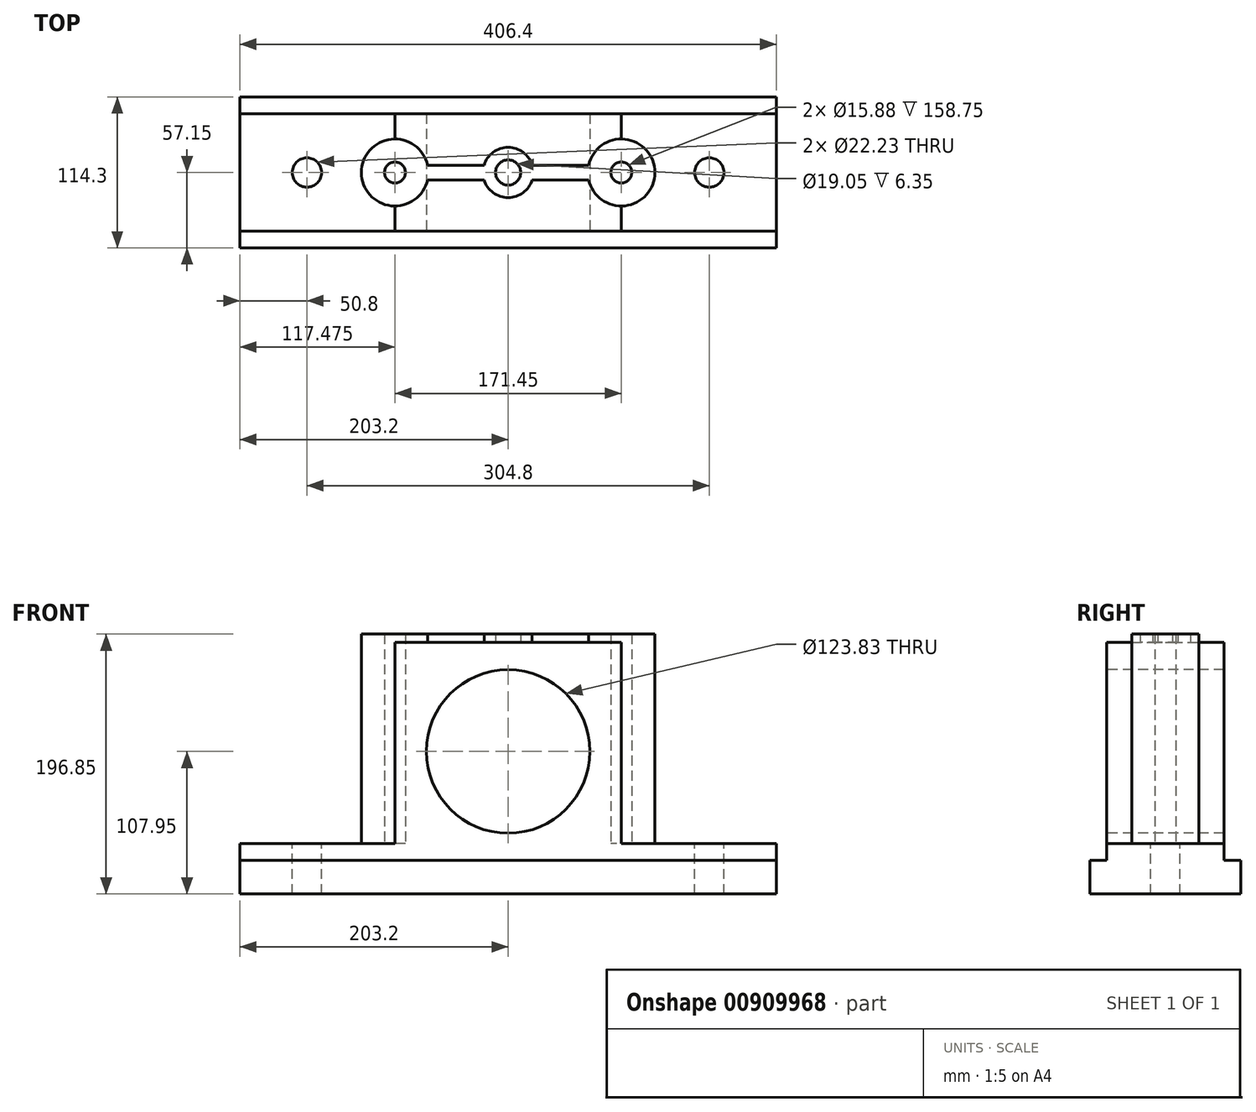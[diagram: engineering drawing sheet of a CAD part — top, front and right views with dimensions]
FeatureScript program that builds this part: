
annotation { "Feature Type Name" : "Feature", "Feature Type Description" : "" }
export const myFeature = defineFeature(function(context is Context, id is Id, definition is map)
    precondition{}
    {
        {
            var Q0;
            Q0=qCreatedBy(makeId("Front.planeOp"),FACE);
            var sketch = newSketch(context, id + "F0", { "sketchPlane" : qUnion([Q0])});
            skLineSegment(sketch, "E0.bottom", {"start": v(-203.2, 0) * mm, "end": v(203.2, 0) * mm});
            skLineSegment(sketch, "E0.top", {"start": v(-203.2, 25.4) * mm, "end": v(203.2, 25.4) * mm});
            skLineSegment(sketch, "E0.left", {"start": v(-203.2, 0) * mm, "end": v(-203.2, 25.4) * mm});
            skLineSegment(sketch, "E0.right", {"start": v(203.2, 0) * mm, "end": v(203.2, 25.4) * mm});
            skLineSegment(sketch, "E1", {"start": v(-203.2, 25.4) * mm, "end": v(-203.2, 38.1) * mm});
            skLineSegment(sketch, "E2", {"start": v(-203.2, 38.1) * mm, "end": v(203.2, 38.1) * mm});
            skLineSegment(sketch, "E3", {"start": v(203.2, 38.1) * mm, "end": v(203.2, 25.4) * mm});
            skLineSegment(sketch, "E4", {"start": v(0, 38.1) * mm, "end": v(0, 0) * mm, "construction": true});
            skCircle(sketch, "E5", {"center": v(0, 107.95) * mm, "radius": 61.91 * mm});
            skSolve(sketch);
        }
        {
            var Q0;
            Q0=makeQuery(id+"F0.imprint","IMPRINT",FACE,{"disambiguationData":[TD([[makeQuery(id+"F0.imprint","IMPRINT",EDGE,{"derivedFrom":sQuery(id+"F0.wireOp",EDGE,"E0.bottom")}),1.0]])]});
            extrude(context, id + "F1", {"entities" : qUnion([Q0]), "depth" : 114.3 * mm, "offsetDistance" : 25 * mm, "symmetric" : true});
        }
        {
            var Q0;
            Q0=makeQuery(id+"F0.imprint","IMPRINT",FACE,{"disambiguationData":[TD([[makeQuery(id+"F0.imprint","IMPRINT",EDGE,{"derivedFrom":sQuery(id+"F0.wireOp",EDGE,"E0.top")}),1.0]])]});
            extrude(context, id + "F2", {"entities" : qUnion([Q0]), "operationType" : NewBodyOperationType.ADD, "depth" : 88.9 * mm, "offsetDistance" : 25 * mm, "symmetric" : true});
        }
        {
            var Q0;
            Q0=makeQuery(id+"F2.opExtrude","SWEPT_FACE",FACE,{"disambiguationData":[OSD([sQuery(id+"F0.wireOp",EDGE,"E2")])]});
            var sketch = newSketch(context, id + "F3", { "sketchPlane" : qUnion([Q0])});
            skLineSegment(sketch, "E6.bottom", {"start": v(-85.72, 44.45) * mm, "end": v(85.72, 44.45) * mm});
            skLineSegment(sketch, "E6.top", {"start": v(-85.72, -44.45) * mm, "end": v(85.72, -44.45) * mm});
            skLineSegment(sketch, "E6.left", {"start": v(-85.72, 44.45) * mm, "end": v(-85.72, -44.45) * mm});
            skLineSegment(sketch, "E6.right", {"start": v(85.72, 44.45) * mm, "end": v(85.72, -44.45) * mm});
            skCircle(sketch, "E7", {"center": v(-85.72, 0) * mm, "radius": 25.4 * mm});
            skCircle(sketch, "E8", {"center": v(85.72, 0) * mm, "radius": 25.4 * mm});
            skCircle(sketch, "E9", {"center": v(0, 0) * mm, "radius": 19.05 * mm});
            skCircle(sketch, "E10", {"center": v(-85.72, 0) * mm, "radius": 7.94 * mm});
            skCircle(sketch, "E11", {"center": v(85.72, 0) * mm, "radius": 7.94 * mm});
            skCircle(sketch, "E12", {"center": v(0, 0) * mm, "radius": 9.53 * mm});
            skLineSegment(sketch, "E13", {"start": v(-60.94, 5.56) * mm, "end": v(-18.22, 5.56) * mm});
            skLineSegment(sketch, "E14", {"start": v(18.22, 5.56) * mm, "end": v(60.94, 5.56) * mm});
            skLineSegment(sketch, "E15", {"start": v(-60.94, -5.56) * mm, "end": v(-18.22, -5.56) * mm});
            skLineSegment(sketch, "E16", {"start": v(18.22, -5.56) * mm, "end": v(60.94, -5.56) * mm});
            skCircle(sketch, "E17", {"center": v(-152.4, 0) * mm, "radius": 11.11 * mm});
            skCircle(sketch, "E18", {"center": v(152.4, 0) * mm, "radius": 11.11 * mm});
            skLineSegment(sketch, "E19", {"start": v(-152.4, 0) * mm, "end": v(0, 0) * mm, "construction": true});
            skLineSegment(sketch, "E20", {"start": v(0, 0) * mm, "end": v(152.4, 0) * mm, "construction": true});
            skLineSegment(sketch, "E21", {"start": v(-69.85, 44.45) * mm, "end": v(-69.85, -44.45) * mm});
            skLineSegment(sketch, "E22", {"start": v(69.85, 44.45) * mm, "end": v(69.85, -44.45) * mm});
            skSolve(sketch);
        }
        {
            var Q0;
            {var subQ0=sQuery(id+"F3.wireOp",EDGE,"E7");var subQ1=sQuery(id+"F3.wireOp",EDGE,"E6.left");var subQ2=makeQuery(id+"F3.imprint","INTERSECT",VERTEX,{"disambiguationData":[OD(0.0)],"derivedFrom":[subQ1,subQ0]});Q0=makeQuery(id+"F3.imprint","IMPRINT",FACE,{"disambiguationData":[TD([[makeQuery(id+"F3.imprint","IMPRINT",EDGE,{"disambiguationData":[TD([[subQ2,-1.0]])],"derivedFrom":subQ1}),-1.0]])]});}
            var Q1;
            {var subQ0=sQuery(id+"F3.wireOp",EDGE,"E7");var subQ2=sQuery(id+"F3.wireOp",EDGE,"E6.left");var subQ4=makeQuery(id+"F3.imprint","INTERSECT",VERTEX,{"disambiguationData":[OD(0.0)],"derivedFrom":[subQ2,subQ0]});Q1=makeQuery(id+"F3.imprint","IMPRINT",FACE,{"disambiguationData":[TD([[makeQuery(id+"F3.imprint","IMPRINT",EDGE,{"disambiguationData":[TD([[subQ4,-1.0]])],"derivedFrom":subQ2}),1.0]])]});}
            var Q2;
            {var subQ0=sQuery(id+"F3.wireOp",EDGE,"E13");Q2=makeQuery(id+"F3.imprint","IMPRINT",FACE,{"disambiguationData":[TD([[makeQuery(id+"F3.imprint","IMPRINT",EDGE,{"derivedFrom":subQ0}),-1.0]])]});}
            var Q3;
            Q3=makeQuery(id+"F3.imprint","IMPRINT",FACE,{"disambiguationData":[TD([[makeQuery(id+"F3.imprint","IMPRINT",EDGE,{"derivedFrom":sQuery(id+"F3.wireOp",EDGE,"E12")}),-1.0]])]});
            var Q4;
            {var subQ0=sQuery(id+"F3.wireOp",EDGE,"E14");Q4=makeQuery(id+"F3.imprint","IMPRINT",FACE,{"disambiguationData":[TD([[makeQuery(id+"F3.imprint","IMPRINT",EDGE,{"derivedFrom":subQ0}),-1.0]])]});}
            var Q5;
            {var subQ0=sQuery(id+"F3.wireOp",EDGE,"E8");var subQ3=sQuery(id+"F3.wireOp",EDGE,"E6.right");var subQ4=makeQuery(id+"F3.imprint","INTERSECT",VERTEX,{"disambiguationData":[OD(0.0)],"derivedFrom":[subQ3,subQ0]});Q5=makeQuery(id+"F3.imprint","IMPRINT",FACE,{"disambiguationData":[TD([[makeQuery(id+"F3.imprint","IMPRINT",EDGE,{"disambiguationData":[TD([[subQ4,-1.0]])],"derivedFrom":subQ3}),-1.0]])]});}
            var Q6;
            {var subQ0=sQuery(id+"F3.wireOp",EDGE,"E8");var subQ1=sQuery(id+"F3.wireOp",EDGE,"E6.right");var subQ2=makeQuery(id+"F3.imprint","INTERSECT",VERTEX,{"disambiguationData":[OD(0.0)],"derivedFrom":[subQ1,subQ0]});Q6=makeQuery(id+"F3.imprint","IMPRINT",FACE,{"disambiguationData":[TD([[makeQuery(id+"F3.imprint","IMPRINT",EDGE,{"disambiguationData":[TD([[subQ2,-1.0]])],"derivedFrom":subQ1}),1.0]])]});}
            var Q7;
            {var subQ0=sQuery(id+"F3.wireOp",EDGE,"E7");var subQ1=makeQuery(id+"F3.imprint","INTERSECT",VERTEX,{"derivedFrom":[subQ0,sQuery(id+"F3.wireOp",EDGE,"E13")]});Q7=makeQuery(id+"F3.imprint","IMPRINT",FACE,{"disambiguationData":[TD([[makeQuery(id+"F3.imprint","IMPRINT",EDGE,{"disambiguationData":[TD([[subQ1,-1.0]])],"derivedFrom":subQ0}),1.0]])]});}
            var Q8;
            {var subQ0=sQuery(id+"F3.wireOp",EDGE,"E8");var subQ1=makeQuery(id+"F3.imprint","INTERSECT",VERTEX,{"derivedFrom":[subQ0,sQuery(id+"F3.wireOp",EDGE,"E14")]});Q8=makeQuery(id+"F3.imprint","IMPRINT",FACE,{"disambiguationData":[TD([[makeQuery(id+"F3.imprint","IMPRINT",EDGE,{"disambiguationData":[TD([[subQ1,1.0]])],"derivedFrom":subQ0}),1.0]])]});}
            extrude(context, id + "F4", {"entities" : qUnion([Q0, Q1, Q2, Q3, Q4, Q5, Q6, Q7, Q8]), "depth" : 158.75 * mm, "offsetDistance" : 25 * mm});
        }
        {
            var Q0;
            {var subQ5=sQuery(id+"F3.wireOp",EDGE,"E6.bottom");Q0=makeQuery(id+"F3.imprint","IMPRINT",FACE,{"disambiguationData":[TD([[makeQuery(id+"F3.imprint","IMPRINT",EDGE,{"derivedFrom":subQ5}),-1.0]])]});}
            var Q1;
            {var subQ5=sQuery(id+"F3.wireOp",EDGE,"E6.top");Q1=makeQuery(id+"F3.imprint","IMPRINT",FACE,{"disambiguationData":[TD([[makeQuery(id+"F3.imprint","IMPRINT",EDGE,{"derivedFrom":subQ5}),1.0]])]});}
            var Q2;
            Q2=makeQuery(id+"F3.imprint","IMPRINT",FACE,{"disambiguationData":[TD([[makeQuery(id+"F3.imprint","IMPRINT",EDGE,{"derivedFrom":sQuery(id+"F3.wireOp",EDGE,"E12")}),1.0]])]});
            var Q3;
            {var subQ0=sQuery(id+"F3.wireOp",EDGE,"E15");Q3=makeQuery(id+"F3.imprint","IMPRINT",FACE,{"disambiguationData":[TD([[makeQuery(id+"F3.imprint","IMPRINT",EDGE,{"derivedFrom":subQ0}),-1.0]])]});}
            var Q4;
            {var subQ0=sQuery(id+"F3.wireOp",EDGE,"E13");Q4=makeQuery(id+"F3.imprint","IMPRINT",FACE,{"disambiguationData":[TD([[makeQuery(id+"F3.imprint","IMPRINT",EDGE,{"derivedFrom":subQ0}),1.0]])]});}
            extrude(context, id + "F5", {"entities" : qUnion([Q0, Q1, Q2, Q3, Q4]), "operationType" : NewBodyOperationType.ADD, "depth" : 152.4 * mm, "offsetDistance" : 25 * mm});
        }
        {
            var Q0;
            {var subQ0=sQuery(id+"F3.wireOp",EDGE,"E13");Q0=makeQuery(id+"F3.imprint","IMPRINT",FACE,{"disambiguationData":[TD([[makeQuery(id+"F3.imprint","IMPRINT",EDGE,{"derivedFrom":subQ0}),1.0]])]});}
            var Q1;
            {var subQ0=sQuery(id+"F3.wireOp",EDGE,"E15");Q1=makeQuery(id+"F3.imprint","IMPRINT",FACE,{"disambiguationData":[TD([[makeQuery(id+"F3.imprint","IMPRINT",EDGE,{"derivedFrom":subQ0}),-1.0]])]});}
            var Q2;
            {var subQ0=sQuery(id+"F3.wireOp",EDGE,"E7");var subQ1=makeQuery(id+"F3.imprint","INTERSECT",VERTEX,{"derivedFrom":[subQ0,sQuery(id+"F3.wireOp",EDGE,"E13")]});Q2=makeQuery(id+"F3.imprint","IMPRINT",FACE,{"disambiguationData":[TD([[makeQuery(id+"F3.imprint","IMPRINT",EDGE,{"disambiguationData":[TD([[subQ1,-1.0]])],"derivedFrom":subQ0}),1.0]])]});}
            var Q3;
            {var subQ0=sQuery(id+"F3.wireOp",EDGE,"E13");Q3=makeQuery(id+"F3.imprint","IMPRINT",FACE,{"disambiguationData":[TD([[makeQuery(id+"F3.imprint","IMPRINT",EDGE,{"derivedFrom":subQ0}),-1.0]])]});}
            var Q4;
            Q4=makeQuery(id+"F3.imprint","IMPRINT",FACE,{"disambiguationData":[TD([[makeQuery(id+"F3.imprint","IMPRINT",EDGE,{"derivedFrom":sQuery(id+"F3.wireOp",EDGE,"E12")}),-1.0]])]});
            var Q5;
            Q5=makeQuery(id+"F3.imprint","IMPRINT",FACE,{"disambiguationData":[TD([[makeQuery(id+"F3.imprint","IMPRINT",EDGE,{"derivedFrom":sQuery(id+"F3.wireOp",EDGE,"E12")}),1.0]])]});
            var Q6;
            {var subQ0=sQuery(id+"F3.wireOp",EDGE,"E14");Q6=makeQuery(id+"F3.imprint","IMPRINT",FACE,{"disambiguationData":[TD([[makeQuery(id+"F3.imprint","IMPRINT",EDGE,{"derivedFrom":subQ0}),-1.0]])]});}
            var Q7;
            {var subQ0=sQuery(id+"F3.wireOp",EDGE,"E8");var subQ1=makeQuery(id+"F3.imprint","INTERSECT",VERTEX,{"derivedFrom":[subQ0,sQuery(id+"F3.wireOp",EDGE,"E14")]});Q7=makeQuery(id+"F3.imprint","IMPRINT",FACE,{"disambiguationData":[TD([[makeQuery(id+"F3.imprint","IMPRINT",EDGE,{"disambiguationData":[TD([[subQ1,1.0]])],"derivedFrom":subQ0}),1.0]])]});}
            extrude(context, id + "F6", {"entities" : qUnion([Q0, Q1, Q2, Q3, Q4, Q5, Q6, Q7]), "operationType" : NewBodyOperationType.REMOVE, "depth" : 69.85 * mm, "offsetDistance" : 25 * mm});
        }
        {
            var Q0;
            {var subQ0=sQuery(id+"F3.wireOp",EDGE,"E6.left");var subQ5=sQuery(id+"F3.wireOp",EDGE,"E7");var subQ6=makeQuery(id+"F3.imprint","INTERSECT",VERTEX,{"disambiguationData":[OD(0.0)],"derivedFrom":[subQ0,subQ5]});Q0=makeQuery(id+"F3.imprint","IMPRINT",FACE,{"disambiguationData":[TD([[makeQuery(id+"F3.imprint","IMPRINT",EDGE,{"disambiguationData":[TD([[subQ6,1.0]])],"derivedFrom":subQ5}),-1.0]])]});}
            var Q1;
            {var subQ0=sQuery(id+"F3.wireOp",EDGE,"E6.left");var subQ5=sQuery(id+"F3.wireOp",EDGE,"E7");var subQ6=makeQuery(id+"F3.imprint","INTERSECT",VERTEX,{"disambiguationData":[OD(1.0)],"derivedFrom":[subQ0,subQ5]});Q1=makeQuery(id+"F3.imprint","IMPRINT",FACE,{"disambiguationData":[TD([[makeQuery(id+"F3.imprint","IMPRINT",EDGE,{"disambiguationData":[TD([[subQ6,-1.0]])],"derivedFrom":subQ5}),-1.0]])]});}
            var Q2;
            {var subQ0=sQuery(id+"F3.wireOp",EDGE,"E7");var subQ1=sQuery(id+"F3.wireOp",EDGE,"E6.left");var subQ7=makeQuery(id+"F3.imprint","INTERSECT",VERTEX,{"disambiguationData":[OD(0.0)],"derivedFrom":[subQ1,subQ0]});Q2=makeQuery(id+"F3.imprint","IMPRINT",FACE,{"disambiguationData":[TD([[makeQuery(id+"F3.imprint","IMPRINT",EDGE,{"disambiguationData":[TD([[subQ7,-1.0]])],"derivedFrom":subQ1}),1.0]])]});}
            var Q3;
            {var subQ0=sQuery(id+"F3.wireOp",EDGE,"E7");var subQ1=sQuery(id+"F3.wireOp",EDGE,"E6.left");var subQ2=makeQuery(id+"F3.imprint","INTERSECT",VERTEX,{"disambiguationData":[OD(0.0)],"derivedFrom":[subQ1,subQ0]});Q3=makeQuery(id+"F3.imprint","IMPRINT",FACE,{"disambiguationData":[TD([[makeQuery(id+"F3.imprint","IMPRINT",EDGE,{"disambiguationData":[TD([[subQ2,-1.0]])],"derivedFrom":subQ1}),-1.0]])]});}
            var Q4;
            {var subQ0=sQuery(id+"F3.wireOp",EDGE,"E8");var subQ1=sQuery(id+"F3.wireOp",EDGE,"E6.right");var subQ2=makeQuery(id+"F3.imprint","INTERSECT",VERTEX,{"disambiguationData":[OD(0.0)],"derivedFrom":[subQ1,subQ0]});Q4=makeQuery(id+"F3.imprint","IMPRINT",FACE,{"disambiguationData":[TD([[makeQuery(id+"F3.imprint","IMPRINT",EDGE,{"disambiguationData":[TD([[subQ2,-1.0]])],"derivedFrom":subQ1}),1.0]])]});}
            var Q5;
            {var subQ0=sQuery(id+"F3.wireOp",EDGE,"E8");var subQ1=sQuery(id+"F3.wireOp",EDGE,"E6.right");var subQ8=makeQuery(id+"F3.imprint","INTERSECT",VERTEX,{"disambiguationData":[OD(0.0)],"derivedFrom":[subQ1,subQ0]});Q5=makeQuery(id+"F3.imprint","IMPRINT",FACE,{"disambiguationData":[TD([[makeQuery(id+"F3.imprint","IMPRINT",EDGE,{"disambiguationData":[TD([[subQ8,-1.0]])],"derivedFrom":subQ1}),-1.0]])]});}
            var Q6;
            {var subQ0=sQuery(id+"F3.wireOp",EDGE,"E6.right");var subQ5=sQuery(id+"F3.wireOp",EDGE,"E8");var subQ6=makeQuery(id+"F3.imprint","INTERSECT",VERTEX,{"disambiguationData":[OD(0.0)],"derivedFrom":[subQ0,subQ5]});Q6=makeQuery(id+"F3.imprint","IMPRINT",FACE,{"disambiguationData":[TD([[makeQuery(id+"F3.imprint","IMPRINT",EDGE,{"disambiguationData":[TD([[subQ6,-1.0]])],"derivedFrom":subQ5}),-1.0]])]});}
            var Q7;
            {var subQ0=sQuery(id+"F3.wireOp",EDGE,"E6.right");var subQ5=sQuery(id+"F3.wireOp",EDGE,"E8");var subQ6=makeQuery(id+"F3.imprint","INTERSECT",VERTEX,{"disambiguationData":[OD(1.0)],"derivedFrom":[subQ0,subQ5]});Q7=makeQuery(id+"F3.imprint","IMPRINT",FACE,{"disambiguationData":[TD([[makeQuery(id+"F3.imprint","IMPRINT",EDGE,{"disambiguationData":[TD([[subQ6,1.0]])],"derivedFrom":subQ5}),-1.0]])]});}
            extrude(context, id + "F7", {"entities" : qUnion([Q0, Q1, Q2, Q3, Q4, Q5, Q6, Q7]), "operationType" : NewBodyOperationType.REMOVE, "depth" : 127 * mm, "offsetDistance" : 25 * mm});
        }
        {
            var Q0;
            {var subQ0=sQuery(id+"F3.wireOp",EDGE,"E6.left");var subQ5=sQuery(id+"F3.wireOp",EDGE,"E7");var subQ6=makeQuery(id+"F3.imprint","INTERSECT",VERTEX,{"disambiguationData":[OD(0.0)],"derivedFrom":[subQ0,subQ5]});Q0=makeQuery(id+"F3.imprint","IMPRINT",FACE,{"disambiguationData":[TD([[makeQuery(id+"F3.imprint","IMPRINT",EDGE,{"disambiguationData":[TD([[subQ6,1.0]])],"derivedFrom":subQ5}),-1.0]])]});}
            var Q1;
            {var subQ0=sQuery(id+"F3.wireOp",EDGE,"E7");var subQ1=sQuery(id+"F3.wireOp",EDGE,"E6.left");var subQ2=makeQuery(id+"F3.imprint","INTERSECT",VERTEX,{"disambiguationData":[OD(0.0)],"derivedFrom":[subQ1,subQ0]});Q1=makeQuery(id+"F3.imprint","IMPRINT",FACE,{"disambiguationData":[TD([[makeQuery(id+"F3.imprint","IMPRINT",EDGE,{"disambiguationData":[TD([[subQ2,-1.0]])],"derivedFrom":subQ1}),-1.0]])]});}
            var Q2;
            {var subQ0=sQuery(id+"F3.wireOp",EDGE,"E7");var subQ1=sQuery(id+"F3.wireOp",EDGE,"E6.left");var subQ7=makeQuery(id+"F3.imprint","INTERSECT",VERTEX,{"disambiguationData":[OD(0.0)],"derivedFrom":[subQ1,subQ0]});Q2=makeQuery(id+"F3.imprint","IMPRINT",FACE,{"disambiguationData":[TD([[makeQuery(id+"F3.imprint","IMPRINT",EDGE,{"disambiguationData":[TD([[subQ7,-1.0]])],"derivedFrom":subQ1}),1.0]])]});}
            var Q3;
            {var subQ0=sQuery(id+"F3.wireOp",EDGE,"E6.left");var subQ5=sQuery(id+"F3.wireOp",EDGE,"E7");var subQ6=makeQuery(id+"F3.imprint","INTERSECT",VERTEX,{"disambiguationData":[OD(1.0)],"derivedFrom":[subQ0,subQ5]});Q3=makeQuery(id+"F3.imprint","IMPRINT",FACE,{"disambiguationData":[TD([[makeQuery(id+"F3.imprint","IMPRINT",EDGE,{"disambiguationData":[TD([[subQ6,-1.0]])],"derivedFrom":subQ5}),-1.0]])]});}
            var Q4;
            {var subQ0=sQuery(id+"F3.wireOp",EDGE,"E6.right");var subQ5=sQuery(id+"F3.wireOp",EDGE,"E8");var subQ6=makeQuery(id+"F3.imprint","INTERSECT",VERTEX,{"disambiguationData":[OD(1.0)],"derivedFrom":[subQ0,subQ5]});Q4=makeQuery(id+"F3.imprint","IMPRINT",FACE,{"disambiguationData":[TD([[makeQuery(id+"F3.imprint","IMPRINT",EDGE,{"disambiguationData":[TD([[subQ6,1.0]])],"derivedFrom":subQ5}),-1.0]])]});}
            var Q5;
            {var subQ0=sQuery(id+"F3.wireOp",EDGE,"E8");var subQ1=sQuery(id+"F3.wireOp",EDGE,"E6.right");var subQ8=makeQuery(id+"F3.imprint","INTERSECT",VERTEX,{"disambiguationData":[OD(0.0)],"derivedFrom":[subQ1,subQ0]});Q5=makeQuery(id+"F3.imprint","IMPRINT",FACE,{"disambiguationData":[TD([[makeQuery(id+"F3.imprint","IMPRINT",EDGE,{"disambiguationData":[TD([[subQ8,-1.0]])],"derivedFrom":subQ1}),-1.0]])]});}
            var Q6;
            {var subQ0=sQuery(id+"F3.wireOp",EDGE,"E8");var subQ1=sQuery(id+"F3.wireOp",EDGE,"E6.right");var subQ2=makeQuery(id+"F3.imprint","INTERSECT",VERTEX,{"disambiguationData":[OD(0.0)],"derivedFrom":[subQ1,subQ0]});Q6=makeQuery(id+"F3.imprint","IMPRINT",FACE,{"disambiguationData":[TD([[makeQuery(id+"F3.imprint","IMPRINT",EDGE,{"disambiguationData":[TD([[subQ2,-1.0]])],"derivedFrom":subQ1}),1.0]])]});}
            var Q7;
            {var subQ0=sQuery(id+"F3.wireOp",EDGE,"E6.right");var subQ5=sQuery(id+"F3.wireOp",EDGE,"E8");var subQ6=makeQuery(id+"F3.imprint","INTERSECT",VERTEX,{"disambiguationData":[OD(0.0)],"derivedFrom":[subQ0,subQ5]});Q7=makeQuery(id+"F3.imprint","IMPRINT",FACE,{"disambiguationData":[TD([[makeQuery(id+"F3.imprint","IMPRINT",EDGE,{"disambiguationData":[TD([[subQ6,-1.0]])],"derivedFrom":subQ5}),-1.0]])]});}
            extrude(context, id + "F8", {"entities" : qUnion([Q0, Q1, Q2, Q3, Q4, Q5, Q6, Q7]), "operationType" : NewBodyOperationType.ADD, "depth" : 127 * mm, "offsetDistance" : 25 * mm});
        }
        {
            var Q0;
            {var subQ0=sQuery(id+"F3.wireOp",EDGE,"E13");Q0=makeQuery(id+"F3.imprint","IMPRINT",FACE,{"disambiguationData":[TD([[makeQuery(id+"F3.imprint","IMPRINT",EDGE,{"derivedFrom":subQ0}),1.0]])]});}
            var Q1;
            {var subQ0=sQuery(id+"F3.wireOp",EDGE,"E7");var subQ1=makeQuery(id+"F3.imprint","INTERSECT",VERTEX,{"derivedFrom":[subQ0,sQuery(id+"F3.wireOp",EDGE,"E13")]});Q1=makeQuery(id+"F3.imprint","IMPRINT",FACE,{"disambiguationData":[TD([[makeQuery(id+"F3.imprint","IMPRINT",EDGE,{"disambiguationData":[TD([[subQ1,-1.0]])],"derivedFrom":subQ0}),1.0]])]});}
            var Q2;
            Q2=makeQuery(id+"F3.imprint","IMPRINT",FACE,{"disambiguationData":[TD([[makeQuery(id+"F3.imprint","IMPRINT",EDGE,{"derivedFrom":sQuery(id+"F3.wireOp",EDGE,"E12")}),-1.0]])]});
            var Q3;
            Q3=makeQuery(id+"F3.imprint","IMPRINT",FACE,{"disambiguationData":[TD([[makeQuery(id+"F3.imprint","IMPRINT",EDGE,{"derivedFrom":sQuery(id+"F3.wireOp",EDGE,"E12")}),1.0]])]});
            var Q4;
            {var subQ0=sQuery(id+"F3.wireOp",EDGE,"E8");var subQ1=makeQuery(id+"F3.imprint","INTERSECT",VERTEX,{"derivedFrom":[subQ0,sQuery(id+"F3.wireOp",EDGE,"E14")]});Q4=makeQuery(id+"F3.imprint","IMPRINT",FACE,{"disambiguationData":[TD([[makeQuery(id+"F3.imprint","IMPRINT",EDGE,{"disambiguationData":[TD([[subQ1,1.0]])],"derivedFrom":subQ0}),1.0]])]});}
            var Q5;
            {var subQ0=sQuery(id+"F3.wireOp",EDGE,"E14");Q5=makeQuery(id+"F3.imprint","IMPRINT",FACE,{"disambiguationData":[TD([[makeQuery(id+"F3.imprint","IMPRINT",EDGE,{"derivedFrom":subQ0}),-1.0]])]});}
            var Q6;
            {var subQ0=sQuery(id+"F3.wireOp",EDGE,"E13");Q6=makeQuery(id+"F3.imprint","IMPRINT",FACE,{"disambiguationData":[TD([[makeQuery(id+"F3.imprint","IMPRINT",EDGE,{"derivedFrom":subQ0}),-1.0]])]});}
            var Q7;
            {var subQ0=sQuery(id+"F3.wireOp",EDGE,"E15");Q7=makeQuery(id+"F3.imprint","IMPRINT",FACE,{"disambiguationData":[TD([[makeQuery(id+"F3.imprint","IMPRINT",EDGE,{"derivedFrom":subQ0}),-1.0]])]});}
            extrude(context, id + "F9", {"entities" : qUnion([Q0, Q1, Q2, Q3, Q4, Q5, Q6, Q7]), "operationType" : NewBodyOperationType.ADD, "depth" : 69.85 * mm, "offsetDistance" : 25 * mm});
        }
        {
            var Q0;
            Q0=makeQuery(id+"F3.imprint","IMPRINT",FACE,{"disambiguationData":[TD([[makeQuery(id+"F3.imprint","IMPRINT",EDGE,{"derivedFrom":sQuery(id+"F3.wireOp",EDGE,"E17")}),1.0]])]});
            var Q1;
            Q1=makeQuery(id+"F3.imprint","IMPRINT",FACE,{"disambiguationData":[TD([[makeQuery(id+"F3.imprint","IMPRINT",EDGE,{"derivedFrom":sQuery(id+"F3.wireOp",EDGE,"E18")}),1.0]])]});
            extrude(context, id + "F10", {"entities" : qUnion([Q0, Q1]), "operationType" : NewBodyOperationType.REMOVE, "endBound" : BoundingType.THROUGH_ALL, "oppositeDirection" : true, "depth" : 25 * mm, "offsetDistance" : 25 * mm});
        }
        {
            var Q0;
            Q0=makeQuery(id+"F0.imprint","IMPRINT",FACE,{"disambiguationData":[TD([[makeQuery(id+"F0.imprint","IMPRINT",EDGE,{"derivedFrom":sQuery(id+"F0.wireOp",EDGE,"E5")}),1.0]])]});
            extrude(context, id + "F11", {"entities" : qUnion([Q0]), "operationType" : NewBodyOperationType.REMOVE, "oppositeDirection" : true, "depth" : 254 * mm, "offsetDistance" : 25 * mm, "symmetric" : true});
        }
    });
